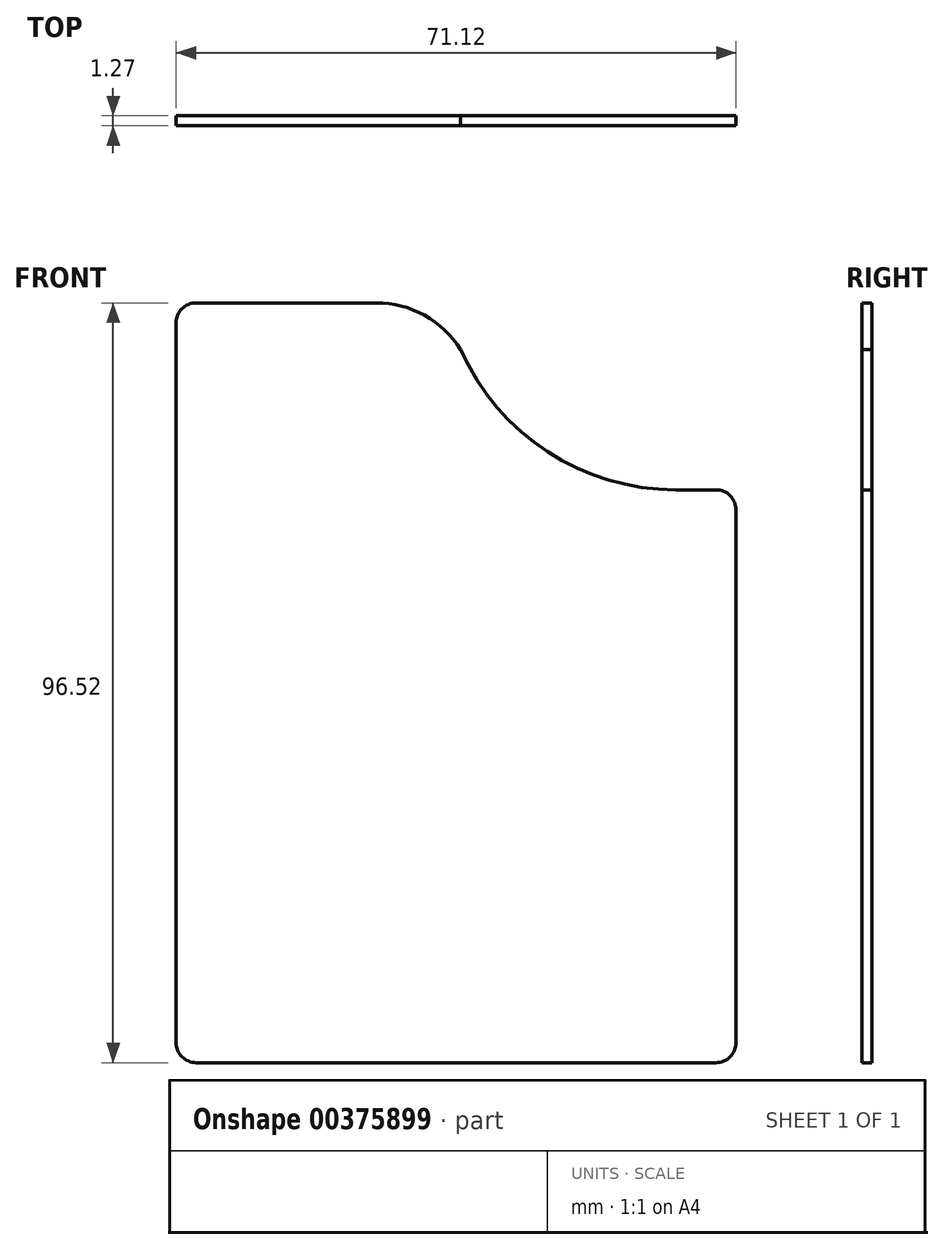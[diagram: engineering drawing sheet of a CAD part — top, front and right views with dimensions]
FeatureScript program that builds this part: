
annotation { "Feature Type Name" : "Feature", "Feature Type Description" : "" }
export const myFeature = defineFeature(function(context is Context, id is Id, definition is map)
    precondition{}
    {
        {
            var Q0;
            Q0=qCreatedBy(makeId("Front.planeOp"),FACE);
            var sketch = newSketch(context, id + "F0", { "sketchPlane" : qUnion([Q0])});
            skLineSegment(sketch, "E0.bottom", {"start": v(-19.61, 57.77) * mm, "end": v(3.25, 57.77) * mm});
            skLineSegment(sketch, "E0.top", {"start": v(-19.61, -38.75) * mm, "end": v(46.43, -38.75) * mm});
            skLineSegment(sketch, "E0.left", {"start": v(-22.15, 55.23) * mm, "end": v(-22.15, -36.2) * mm});
            skLineSegment(sketch, "E0.right", {"start": v(48.97, 31.48) * mm, "end": v(48.97, -36.2) * mm});
            skPoint(sketch, "E1.visualSharp", {"position": v(10.95, 57.77) * mm});
            skArc(sketch, "E1.filletArc", {"start": v(14, 51.84) * mm, "mid": v(9.39, 56.2) * mm, "end": v(3.25, 57.77) * mm});
            skLineSegment(sketch, "E2", {"start": v(46.43, 34.02) * mm, "end": v(41.35, 34.02) * mm});
            skArc(sketch, "E3", {"start": v(14, 51.84) * mm, "mid": v(25.02, 38.87) * mm, "end": v(41.35, 34.02) * mm});
            skPoint(sketch, "E4.visualSharp", {"position": v(-22.15, -38.75) * mm});
            skArc(sketch, "E4.filletArc", {"start": v(-22.15, -36.2) * mm, "mid": v(-21.4, -38) * mm, "end": v(-19.61, -38.75) * mm});
            skPoint(sketch, "E5.visualSharp", {"position": v(48.97, -38.75) * mm});
            skArc(sketch, "E5.filletArc", {"start": v(46.43, -38.75) * mm, "mid": v(48.22, -38) * mm, "end": v(48.97, -36.2) * mm});
            skPoint(sketch, "E6.visualSharp", {"position": v(-22.15, 57.77) * mm});
            skArc(sketch, "E6.filletArc", {"start": v(-19.61, 57.77) * mm, "mid": v(-21.4, 57.03) * mm, "end": v(-22.15, 55.23) * mm});
            skPoint(sketch, "E7.visualSharp", {"position": v(48.97, 34.02) * mm});
            skArc(sketch, "E7.filletArc", {"start": v(48.97, 31.48) * mm, "mid": v(48.22, 33.27) * mm, "end": v(46.43, 34.02) * mm});
            skLineSegment(sketch, "E8", {"start": v(-10.72, 26.02) * mm, "end": v(37.54, 15.86) * mm});
            skSolve(sketch);
        }
        {
            var Q0;
            Q0=makeQuery(id+"F0.imprint","IMPRINT",FACE,{"disambiguationData":[TD([[makeQuery(id+"F0.imprint","IMPRINT",EDGE,{"derivedFrom":sQuery(id+"F0.wireOp",EDGE,"E0.bottom")}),-1.0]])]});
            extrude(context, id + "F1", {"entities" : qUnion([Q0]), "depth" : 1.27 * mm});
        }
    });
